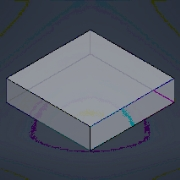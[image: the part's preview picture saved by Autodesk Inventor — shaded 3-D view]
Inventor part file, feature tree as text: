
AUTODESK INVENTOR PART (.ipt)
format: ipt  version: 2024.3 (Build 283343000, 343)  size: 134,656 bytes
history: native  units: mm
features: extrude x1, sketch x1
ambient origin geometry x8: Origin, YZ Plane, XZ Plane, XY Plane, X Axis, Y Axis, Z Axis, Center Point
bodies: Solid1 (feature_tree)
feature tree (2):
  extrude  "Extrusion1"  Depth=100.0mm
  sketch  "Sketch1"  dims[d0=100.0mm d1=100.0mm d2=60.0mm d3=0.0mm]
